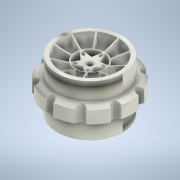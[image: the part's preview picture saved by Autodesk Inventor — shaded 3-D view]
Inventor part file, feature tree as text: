
AUTODESK INVENTOR PART (.ipt)
format: ipt  version: 2022 (Build 260153000, 153)  size: 631,808 bytes
history: native  units: mm
features: chamfer x31, extrude x10, sketch x10, fillet x1
ambient origin geometry x8: Origin, YZ Plane, XZ Plane, XY Plane, X Axis, Y Axis, Z Axis, Center Point
bodies: Solid1 (feature_tree)
feature tree (52):
  extrude  "Extrusion1"  Depth=25.0mm TaperAngle=0.0deg
  extrude  "Extrusion4"  Depth=100.0mm
  extrude  "Extrusion5"  Depth=100.0mm TaperAngle=360.0deg
  extrude  "Extrusion6"  Depth=32.0mm
  chamfer  "Chamfer1"  Distance=8.5mm
  chamfer  "Chamfer2"  Distance=8.5mm
  chamfer  "Chamfer3"  Distance=1.0mm Angle=45.0deg
  chamfer  "Chamfer4"  Distance=1.0mm Angle=45.0deg
  chamfer  "Chamfer5"  Distance=1.0mm Angle=45.0deg
  chamfer  "Chamfer6"  Distance=1.0mm Angle=45.0deg
  chamfer  "Chamfer7"  Distance=1.0mm Angle=45.0deg
  chamfer  "Chamfer8"  Distance=1.0mm Angle=45.0deg
  chamfer  "Chamfer9"  Distance=1.0mm Angle=45.0deg
  chamfer  "Chamfer10"  Distance=1.0mm Angle=45.0deg
  chamfer  "Chamfer11"  Distance=1.0mm Angle=45.0deg
  chamfer  "Chamfer12"  Distance=1.0mm Angle=45.0deg
  chamfer  "Chamfer13"  Distance=1.0mm Angle=45.0deg
  chamfer  "Chamfer14"  Distance=1.0mm Angle=45.0deg
  chamfer  "Chamfer15"  Distance=1.0mm Angle=45.0deg
  chamfer  "Chamfer16"  Distance=1.0mm Angle=45.0deg
  chamfer  "Chamfer17"  Distance=1.0mm Angle=45.0deg
  chamfer  "Chamfer18"  Distance=1.0mm Angle=45.0deg
  chamfer  "Chamfer19"  Distance=1.0mm Angle=45.0deg
  chamfer  "Chamfer20"  Distance=1.0mm Angle=45.0deg
  extrude  "Extrusion7"  Depth=1.0mm TaperAngle=45.0deg
  extrude  "Extrusion8"  TaperAngle=0.0deg  [1 undecoded]
  extrude  "Extrusion9"  Depth=50.0mm TaperAngle=360.0deg
  extrude  "Extrusion10"  Depth=13.5mm
  chamfer  "Chamfer21"  Distance=2.0mm
  chamfer  "Chamfer22"  Distance=100.0mm Angle=360.0deg
  chamfer  "Chamfer23"  Distance=4.2mm
  chamfer  "Chamfer24"  Distance=3.6mm
  chamfer  "Chamfer25"  Distance=12.0mm
  chamfer  "Chamfer26"  Distance=4.0mm
  chamfer  "Chamfer27"  Distance=2.5mm
  chamfer  "Chamfer28"  Distance=1.5mm Angle=45.0deg
  chamfer  "Chamfer29"  Distance=6.75mm Angle=45.0deg
  chamfer  "Chamfer30"  Distance=6.75mm Angle=45.0deg
  chamfer  "Chamfer31"  Distance=6.75mm Angle=45.0deg
  fillet  "Fillet2"  Radius=6.75mm
  extrude  "Extrusion11"  Depth=5.0mm TaperAngle=45.0deg
  extrude  "Extrusion12"  Depth=5.0mm TaperAngle=45.0deg
  sketch  "Sketch1"  dims[d0=40.0mm d1=25.0mm d2=0.0mm]
  sketch  "Sketch4"  dims[d18=100.0mm d21=100.0mm d27=100.0mm d29=100.0mm]
  sketch  "Sketch5"  dims[d30=17.5mm d33=100.0mm d35=360.0deg]
  sketch  "Sketch6"  dims[d37=0.0mm d38=0.0mm d39=32.0mm d40=8.5mm d41=0.0mm]
  sketch  "Sketch7"  dims[d42=32.0mm d43=8.5mm d44=0.0mm d45=1.0mm d46=2.5mm d47=45.0deg d48=1.0mm d49=2.5mm d50=45.0deg d51=1.0mm d52=2.5mm d53=45.0deg d54=1.0mm d55=2.5mm d56=45.0deg d57=1.0mm d58=2.5mm d59=45.0deg d60=1.0mm d61=2.5mm d62=45.0deg d63=1.0mm d64=2.5mm d65=45.0deg d66=1.0mm d67=2.5mm d68=45.0deg d69=1.0mm d70=2.5mm d71=45.0deg d72=1.0mm d73=2.5mm d74=45.0deg d75=1.0mm d76=2.5mm d77=45.0deg d78=1.0mm d79=2.5mm d80=45.0deg d81=1.0mm d82=2.5mm d83=45.0deg d84=1.0mm d85=2.5mm d86=45.0deg d87=1.0mm d88=2.5mm d89=45.0deg d90=1.0mm d91=2.5mm d92=45.0deg d93=1.0mm d94=2.5mm d95=45.0deg d96=1.0mm d97=2.5mm d98=45.0deg]
  sketch  "Sketch8"  dims[d99=1.0mm d100=2.5mm d101=45.0deg d102=1.0mm d103=2.5mm d104=45.0deg]
  sketch  "Sketch9"  dims[d105=28.0mm d106=0.0mm d107=0.0mm]
  sketch  "Sketch10"  dims[d109=7.0mm d110=50.0mm d112=360.0deg]
  sketch  "Sketch14"  dims[d114=50.0mm d116=360.0deg d118=13.5mm]
  sketch  "Sketch15"  dims[d119=14.5mm d120=2.0mm d123=100.0mm d125=360.0deg d128=4.2mm d129=3.6mm d130=12.0mm d131=0.0mm d132=4.0mm d133=0.0mm d134=2.5mm d135=0.0mm d136=1.5mm d137=6.25mm d138=45.0deg d139=6.75mm d140=2.5mm d141=45.0deg d142=6.75mm d143=2.5mm d144=45.0deg d145=6.75mm d146=2.5mm d147=45.0deg d148=6.75mm d149=2.5mm d150=45.0deg d151=6.75mm d152=2.5mm d153=45.0deg d154=6.75mm d155=2.5mm d156=45.0deg d157=6.75mm d158=2.5mm d159=45.0deg d160=6.75mm d161=2.5mm d162=45.0deg d163=6.75mm d164=2.5mm d165=45.0deg d166=6.75mm d167=2.5mm d168=45.0deg d169=1.0mm d170=5.0mm d171=0.0mm d172=5.0mm d173=0.0mm]
note: 1 required parameter value undecoded (feature->parameter linkage not recoverable at this tier; creation-order binding heuristic only, values carry confidence <= 0.55)
